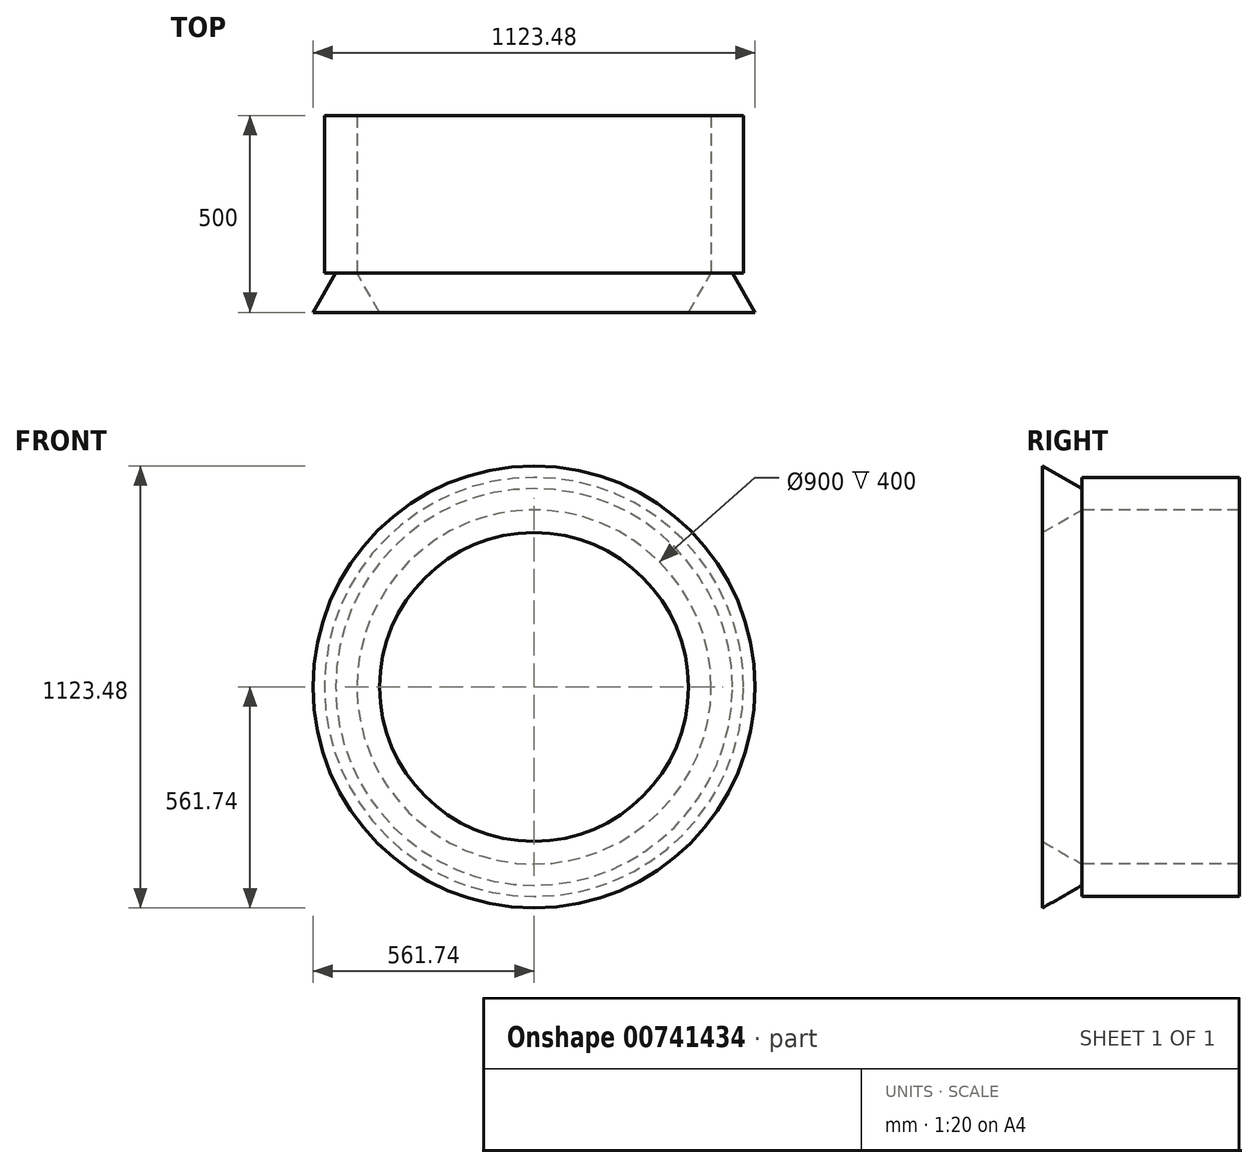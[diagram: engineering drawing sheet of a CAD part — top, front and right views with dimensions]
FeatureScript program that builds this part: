
annotation { "Feature Type Name" : "Feature", "Feature Type Description" : "" }
export const myFeature = defineFeature(function(context is Context, id is Id, definition is map)
    precondition{}
    {
        {
            var Q0;
            Q0=qCreatedBy(makeId("Front.planeOp"),FACE);
            var sketch = newSketch(context, id + "F0", { "sketchPlane" : qUnion([Q0])});
            skCircle(sketch, "E0", {"center": v(0, 0) * mm, "radius": 532.5 * mm});
            skSolve(sketch);
        }
        {
            var Q0;
            Q0=makeQuery(id+"F0.imprint","IMPRINT",FACE,{"disambiguationData":[TD([[makeQuery(id+"F0.imprint","IMPRINT",EDGE,{"derivedFrom":sQuery(id+"F0.wireOp",EDGE,"E0")}),1.0]])]});
            extrude(context, id + "F1", {"entities" : qUnion([Q0]), "depth" : 400 * mm, "offsetDistance" : 25 * mm});
        }
        {
            var Q0;
            Q0=makeQuery(id+"F1.opExtrude","CAP_FACE",FACE,{"disambiguationData":[OSD([sQuery(id+"F0.wireOp",EDGE,"E0")])],"isStart":false});
            var sketch = newSketch(context, id + "F2", { "sketchPlane" : qUnion([Q0])});
            skCircle(sketch, "E1", {"center": v(0, 0) * mm, "radius": 450 * mm});
            skSolve(sketch);
        }
        {
            var Q0;
            Q0=makeQuery(id+"F2.imprint","IMPRINT",FACE,{"disambiguationData":[TD([[makeQuery(id+"F2.imprint","IMPRINT",EDGE,{"derivedFrom":sQuery(id+"F2.wireOp",EDGE,"E1")}),1.0]])]});
            extrude(context, id + "F3", {"entities" : qUnion([Q0]), "operationType" : NewBodyOperationType.REMOVE, "oppositeDirection" : true, "depth" : 400 * mm, "offsetDistance" : 25 * mm});
        }
        {
            var Q0;
            Q0=makeQuery(id+"F1.opExtrude","CAP_FACE",FACE,{"disambiguationData":[OSD([sQuery(id+"F0.wireOp",EDGE,"E0")])],"isStart":false});
            var sketch = newSketch(context, id + "F4", { "sketchPlane" : qUnion([Q0])});
            skCircle(sketch, "E2", {"center": v(0, 0) * mm, "radius": 504 * mm});
            skSolve(sketch);
        }
        {
            var Q0;
            Q0=makeQuery(id+"F4.imprint","IMPRINT",FACE,{"disambiguationData":[TD([[makeQuery(id+"F4.imprint","IMPRINT",EDGE,{"derivedFrom":sQuery(id+"F4.wireOp",EDGE,"E2")}),1.0]])]});
            extrude(context, id + "F5", {"entities" : qUnion([Q0]), "operationType" : NewBodyOperationType.ADD, "depth" : 100 * mm, "offsetDistance" : 25 * mm, "hasDraft" : true, "draftAngle" : 30 * degree});
        }
    });
